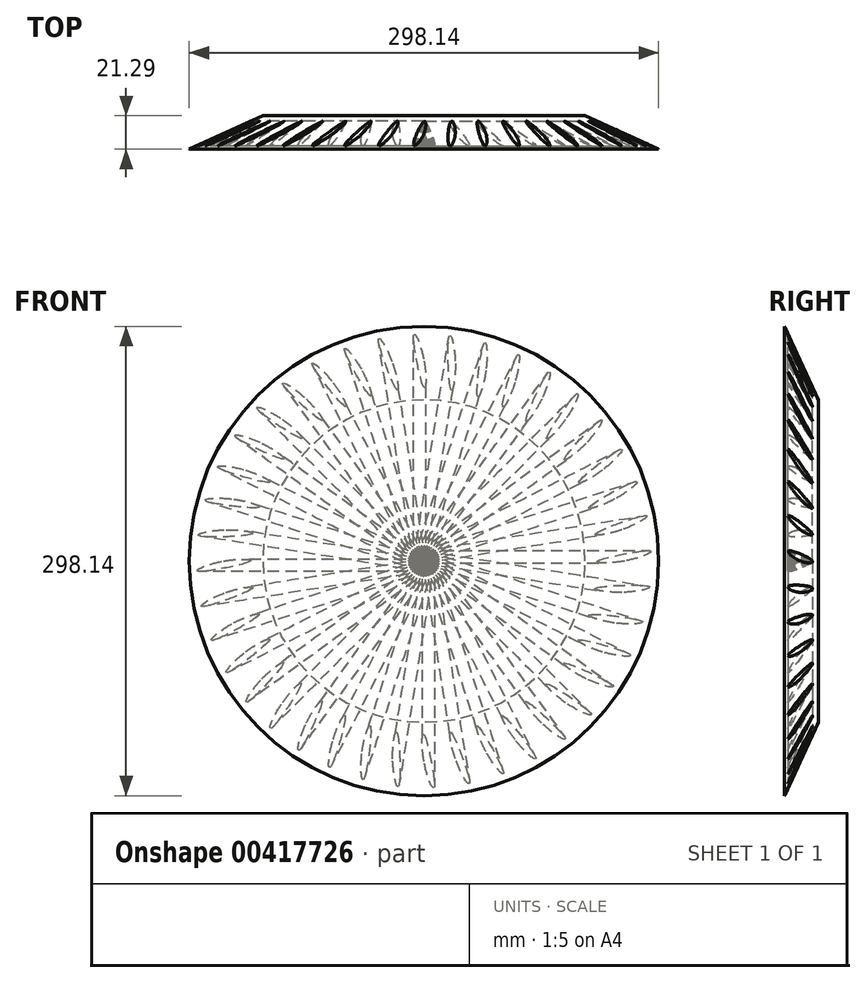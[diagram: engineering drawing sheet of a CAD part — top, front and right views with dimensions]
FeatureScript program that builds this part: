
annotation { "Feature Type Name" : "Feature", "Feature Type Description" : "" }
export const myFeature = defineFeature(function(context is Context, id is Id, definition is map)
    precondition{}
    {
        {
            var Q0;
            Q0=qCreatedBy(makeId("Top.planeOp"),FACE);
            var sketch = newSketch(context, id + "F0", { "sketchPlane" : qUnion([Q0])});
            skLineSegment(sketch, "E0", {"start": v(0, 0) * mm, "end": v(0, 21.3) * mm});
            skLineSegment(sketch, "E1", {"start": v(0, 21.3) * mm, "end": v(102.36, 21.3) * mm});
            skLineSegment(sketch, "E2", {"start": v(102.36, 21.3) * mm, "end": v(149.07, 0) * mm});
            skLineSegment(sketch, "E3", {"start": v(149.07, 0) * mm, "end": v(0, 0) * mm});
            skSolve(sketch);
        }
        {
            var Q0;
            Q0=makeQuery(id+"F0.imprint","IMPRINT",FACE,{"disambiguationData":[TD([[makeQuery(id+"F0.imprint","IMPRINT",EDGE,{"derivedFrom":sQuery(id+"F0.wireOp",EDGE,"E0")}),-1.0]])]});
            var Q1;
            Q1=sQuery(id+"F0.wireOp",EDGE,"E0");
            revolve(context, id + "F1", {"entities" : qUnion([Q0]), "axis" : qUnion([Q1]), "revolveType" : RevolveType.FULL});
        }
        {
            var Q0;
            Q0=qCreatedBy(makeId("Top.planeOp"),FACE);
            var sketch = newSketch(context, id + "F2", { "sketchPlane" : qUnion([Q0])});
            skFitSpline(sketch, "E4", {"points": [v(0, 17.7) * mm, v(6.54, 2.5) * mm, v(0, 9.97) * mm, v(0, 17.7) * mm]});
            skSolve(sketch);
        }
        {
            var Q0;
            Q0 = qSketchRegion(id + "F2", true);
            extrude(context, id + "F3", {"entities" : qUnion([Q0]), "operationType" : NewBodyOperationType.REMOVE, "endBound" : BoundingType.THROUGH_ALL, "oppositeDirection" : true, "depth" : 25.4 * mm});
        }
        {
            var Q0;
            Q0=makeQuery(id+"F1.opRevolve","SWEPT_BODY",BODY,{"disambiguationData":[OSD([sQuery(id+"F0.wireOp",EDGE,"E0"),sQuery(id+"F0.wireOp",EDGE,"E1"),sQuery(id+"F0.wireOp",EDGE,"E2"),sQuery(id+"F0.wireOp",EDGE,"E3")])]});
            var Q1;
            Q1=makeQuery(id+"F1.opRevolve","SWEPT_EDGE",EDGE,{"disambiguationData":[OSD([sQuery(id+"F0.wireOp",EDGE,"E2"),sQuery(id+"F0.wireOp",EDGE,"E3")])]});
            circularPattern(context, id + "F4", {"entities" : qUnion([Q0]), "axis" : qUnion([Q1]), "angle" : 360 * degree, "instanceCount" : 40, "equalSpace" : true});
        }
    });
